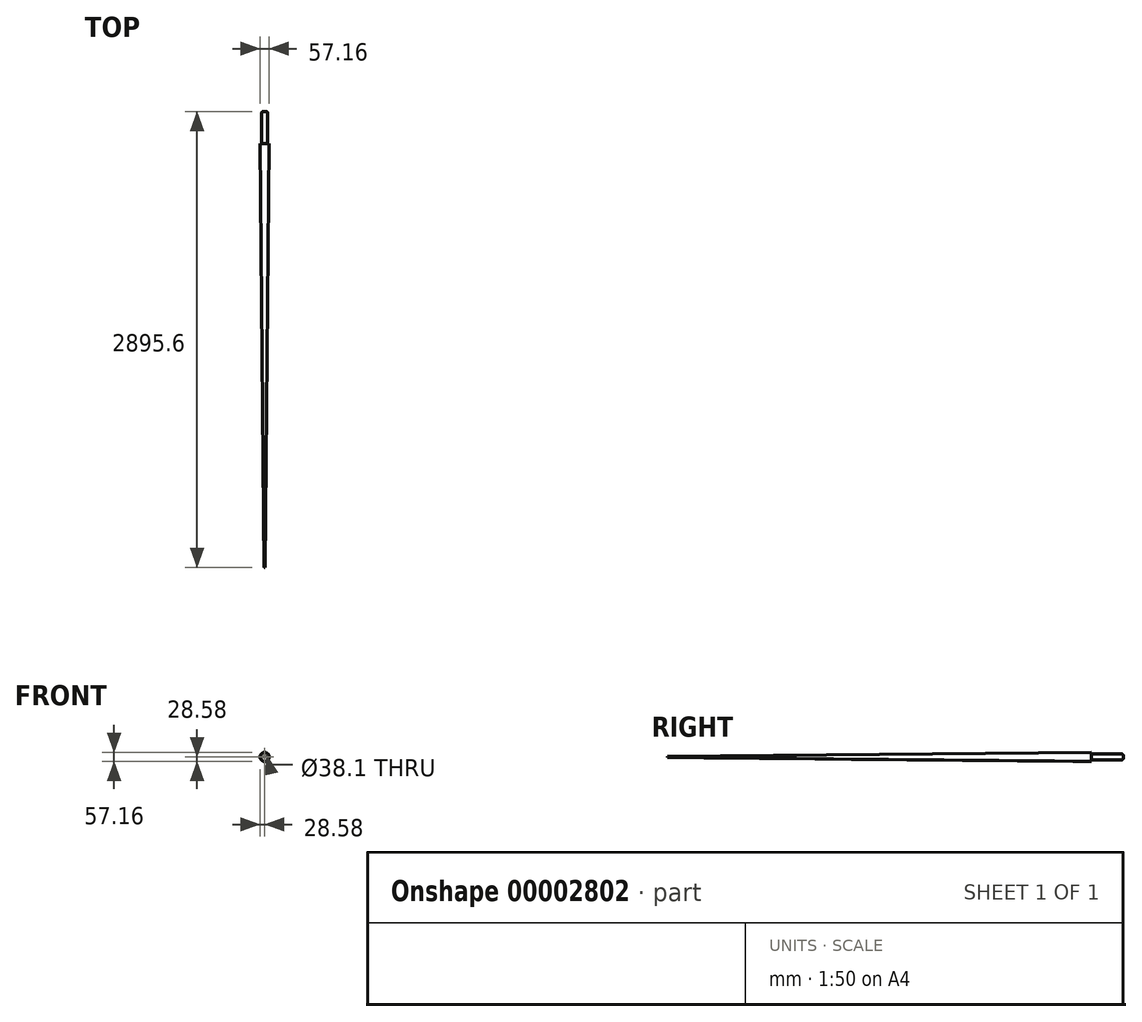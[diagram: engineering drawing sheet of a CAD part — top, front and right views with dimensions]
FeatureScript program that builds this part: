
annotation { "Feature Type Name" : "Feature", "Feature Type Description" : "" }
export const myFeature = defineFeature(function(context is Context, id is Id, definition is map)
    precondition{}
    {
        {
            var Q0;
            Q0=qCreatedBy(makeId("Top.planeOp"),FACE);
            var sketch = newSketch(context, id + "F0", { "sketchPlane" : qUnion([Q0])});
            skLineSegment(sketch, "E0", {"start": v(0, 1418.08) * mm, "end": v(0, -1477.52) * mm});
            skLineSegment(sketch, "E1", {"start": v(0, 1418.08) * mm, "end": v(19.05, 1418.08) * mm});
            skLineSegment(sketch, "E2", {"start": v(19.05, 1418.08) * mm, "end": v(19.05, 1214.88) * mm});
            skLineSegment(sketch, "E3", {"start": v(19.05, 1214.88) * mm, "end": v(0, 1214.88) * mm});
            skLineSegment(sketch, "E4", {"start": v(0, 1214.88) * mm, "end": v(28.58, 1214.88) * mm});
            skLineSegment(sketch, "E5", {"start": v(0, -1477.52) * mm, "end": v(3.18, -1477.52) * mm});
            skLineSegment(sketch, "E6", {"start": v(3.18, -1477.52) * mm, "end": v(28.58, 1214.88) * mm});
            skSolve(sketch);
        }
        {
            var Q0;
            Q0=sQuery(id+"F0.wireOp",EDGE,"E2");
            var Q1;
            Q1=sQuery(id+"F0.wireOp",EDGE,"E6");
            var Q2;
            Q2=sQuery(id+"F0.wireOp",EDGE,"E1");
            var Q3;
            Q3=sQuery(id+"F0.wireOp",EDGE,"E0");
            revolve(context, id + "F1", {"bodyType" : ToolBodyType.SURFACE, "surfaceEntities" : qUnion([Q0, Q1, Q2]), "axis" : qUnion([Q3]), "revolveType" : RevolveType.FULL});
        }
        {
            var Q0;
            Q0=makeQuery(id+"F1.opRevolve","SWEPT_FACE",FACE,{"disambiguationData":[OSD([sQuery(id+"F0.wireOp",EDGE,"E2")])]});
            fillet(context, id + "F2", {"entities" : qUnion([Q0]), "radius" : 9.52 * mm, "tangentPropagation" : true, "allowEdgeOverflow" : false});
        }
    });
